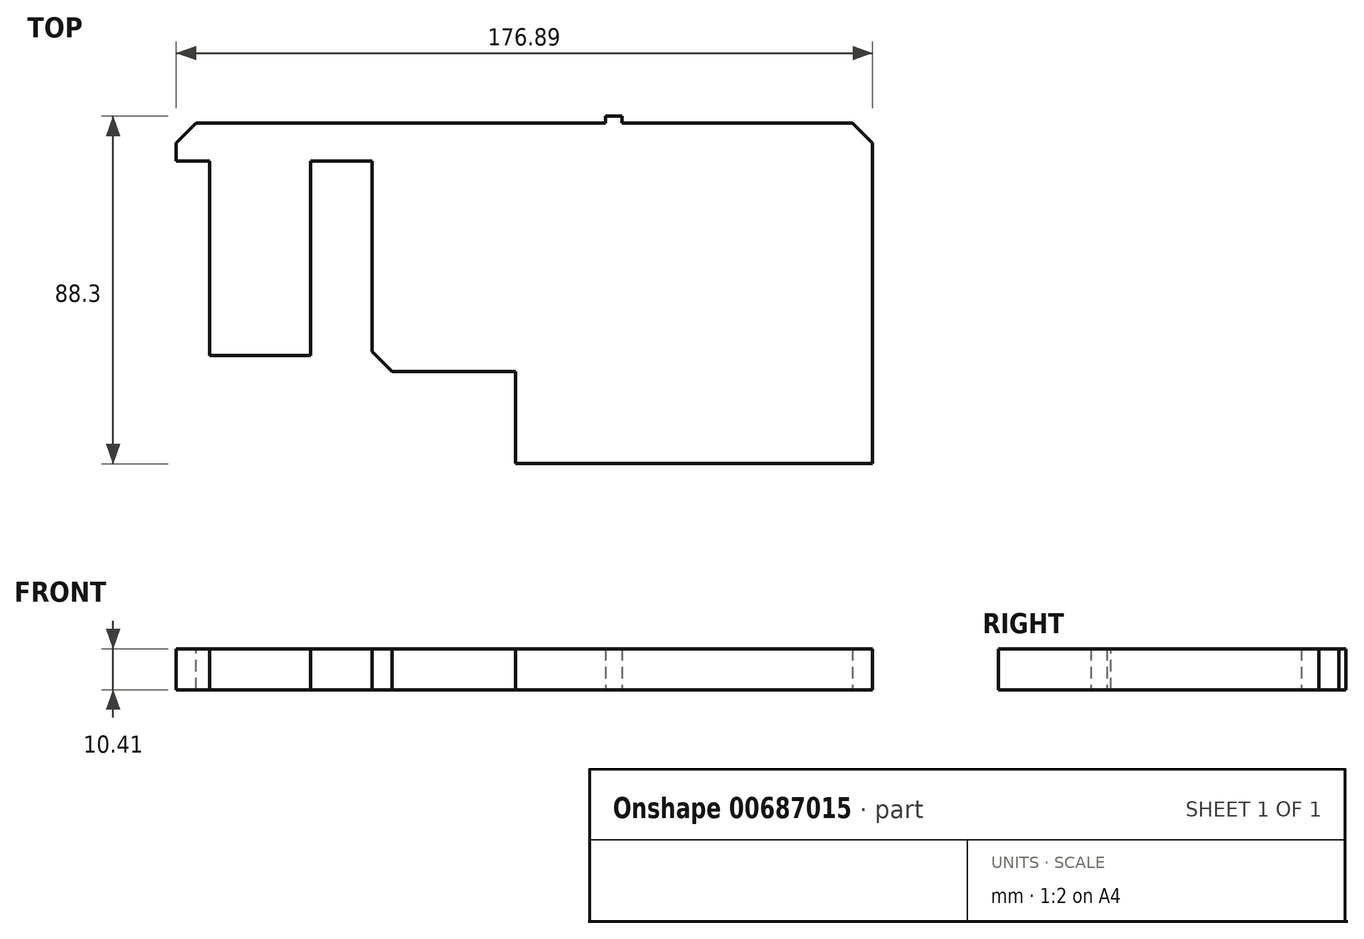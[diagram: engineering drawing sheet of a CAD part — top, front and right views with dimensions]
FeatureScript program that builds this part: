
annotation { "Feature Type Name" : "Feature", "Feature Type Description" : "" }
export const myFeature = defineFeature(function(context is Context, id is Id, definition is map)
    precondition{}
    {
        {
            var Q0;
            Q0=qCreatedBy(makeId("Top.planeOp"),FACE);
            var sketch = newSketch(context, id + "F0", { "sketchPlane" : qUnion([Q0])});
            skLineSegment(sketch, "E0.bottom", {"start": v(-36.36, 24.34) * mm, "end": v(27.1, 24.34) * mm});
            skLineSegment(sketch, "E0.top", {"start": v(-36.36, -38.72) * mm, "end": v(27.1, -38.72) * mm});
            skLineSegment(sketch, "E0.left", {"start": v(-36.36, 24.34) * mm, "end": v(-36.36, -38.72) * mm});
            skLineSegment(sketch, "E0.right", {"start": v(27.1, 24.34) * mm, "end": v(27.1, -38.72) * mm});
            skLineSegment(sketch, "E1.bottom", {"start": v(27.1, 24.34) * mm, "end": v(22.96, 24.34) * mm});
            skLineSegment(sketch, "E1.top", {"start": v(27.1, 26.11) * mm, "end": v(22.96, 26.11) * mm});
            skLineSegment(sketch, "E1.left", {"start": v(27.1, 24.34) * mm, "end": v(27.1, 26.11) * mm});
            skLineSegment(sketch, "E1.right", {"start": v(22.96, 24.34) * mm, "end": v(22.96, 26.11) * mm});
            skLineSegment(sketch, "E2.bottom", {"start": v(-30.37, 24.34) * mm, "end": v(0, 24.34) * mm});
            skLineSegment(sketch, "E2.top", {"start": v(-30.37, -26.02) * mm, "end": v(0, -26.02) * mm});
            skLineSegment(sketch, "E2.left", {"start": v(-30.37, 24.34) * mm, "end": v(-30.37, -26.02) * mm});
            skLineSegment(sketch, "E2.right", {"start": v(0, 24.34) * mm, "end": v(0, -26.02) * mm});
            skLineSegment(sketch, "E3.bottom", {"start": v(0, 24.34) * mm, "end": v(90.72, 24.34) * mm});
            skLineSegment(sketch, "E3.top", {"start": v(0, -62.19) * mm, "end": v(90.72, -62.19) * mm});
            skLineSegment(sketch, "E3.left", {"start": v(0, 24.34) * mm, "end": v(0, -62.19) * mm});
            skLineSegment(sketch, "E3.right", {"start": v(90.72, 24.34) * mm, "end": v(90.72, -62.19) * mm});
            skLineSegment(sketch, "E4.bottom", {"start": v(-36.36, 14.72) * mm, "end": v(-86.17, 14.72) * mm});
            skLineSegment(sketch, "E4.top", {"start": v(-36.36, 24.34) * mm, "end": v(-86.17, 24.34) * mm});
            skLineSegment(sketch, "E4.left", {"start": v(-36.36, 14.72) * mm, "end": v(-36.36, 24.34) * mm});
            skLineSegment(sketch, "E4.right", {"start": v(-86.17, 14.72) * mm, "end": v(-86.17, 24.34) * mm});
            skLineSegment(sketch, "E5.bottom", {"start": v(-77.7, 14.72) * mm, "end": v(-52.08, 14.72) * mm});
            skLineSegment(sketch, "E5.top", {"start": v(-77.7, -34.65) * mm, "end": v(-52.08, -34.65) * mm});
            skLineSegment(sketch, "E5.left", {"start": v(-77.7, 14.72) * mm, "end": v(-77.7, -34.65) * mm});
            skLineSegment(sketch, "E5.right", {"start": v(-52.08, 14.72) * mm, "end": v(-52.08, -34.65) * mm});
            skSolve(sketch);
        }
        {
            var Q0;
            Q0 = qSketchRegion(id + "F0", true);
            extrude(context, id + "F1", {"entities" : qUnion([Q0]), "depth" : 10.4 * mm, "offsetDistance" : 25.4 * mm});
        }
        {
            var Q0;
            Q0=makeQuery(id+"F1.opExtrude","SWEPT_EDGE",EDGE,{"disambiguationData":[OSD([sQuery(id+"F0.wireOp",EDGE,"E4.top"),sQuery(id+"F0.wireOp",EDGE,"E4.right")])]});
            var Q1;
            Q1=makeQuery(id+"F1.opExtrude","SWEPT_EDGE",EDGE,{"disambiguationData":[OSD([sQuery(id+"F0.wireOp",EDGE,"E0.top"),sQuery(id+"F0.wireOp",EDGE,"E0.left")])]});
            var Q2;
            Q2=makeQuery(id+"F1.opExtrude","SWEPT_EDGE",EDGE,{"disambiguationData":[OSD([sQuery(id+"F0.wireOp",EDGE,"E3.bottom"),sQuery(id+"F0.wireOp",EDGE,"E3.right")])]});
            chamfer(context, id + "F2", {"entities" : qUnion([Q0, Q1, Q2]), "width" : 5.08 * mm, "tangentPropagation" : true});
        }
    });
